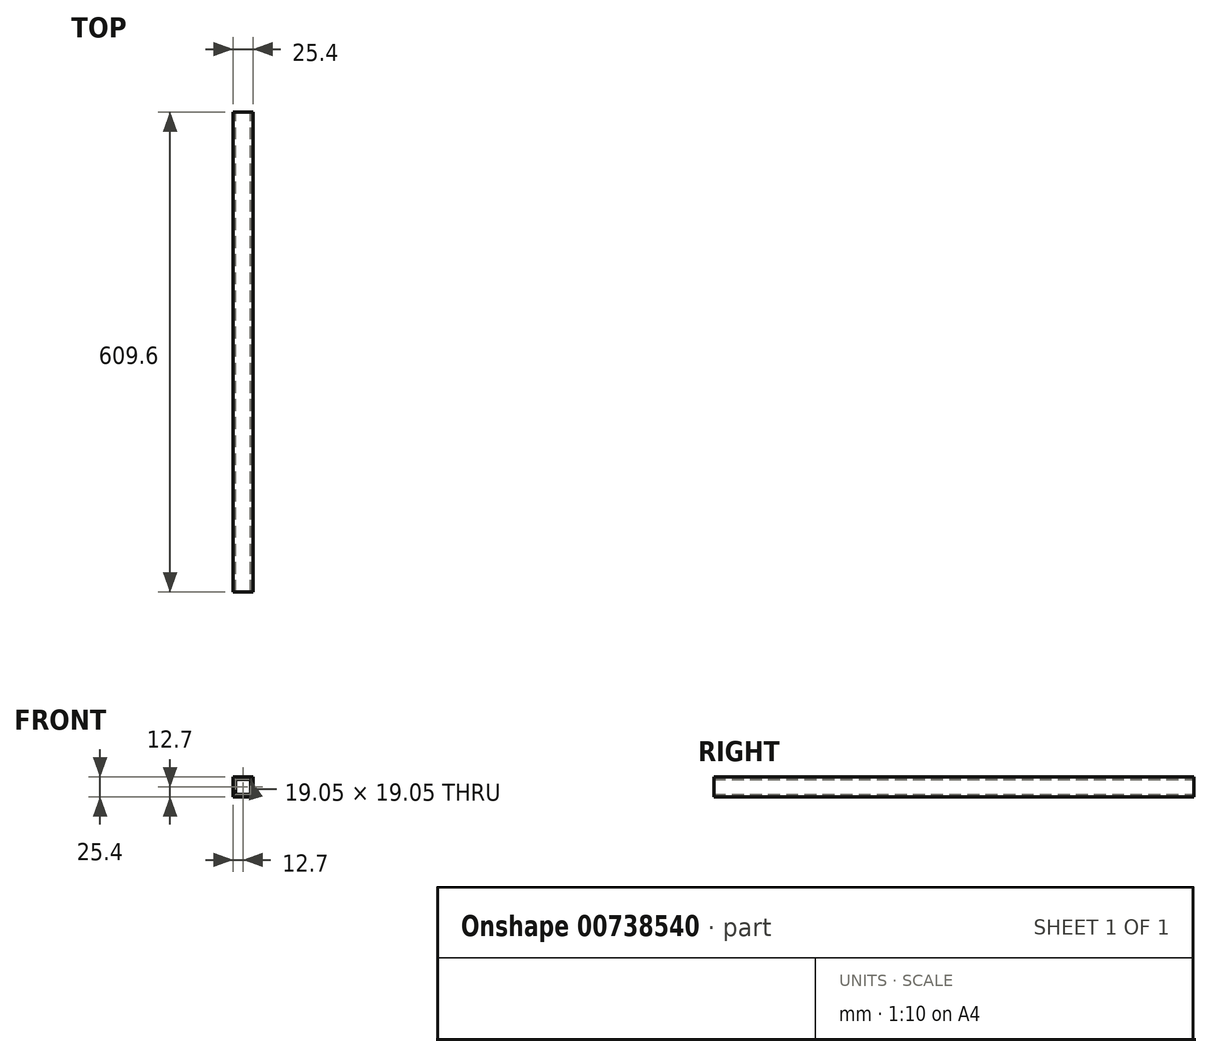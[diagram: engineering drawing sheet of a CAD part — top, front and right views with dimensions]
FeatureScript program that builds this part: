
annotation { "Feature Type Name" : "Feature", "Feature Type Description" : "" }
export const myFeature = defineFeature(function(context is Context, id is Id, definition is map)
    precondition{}
    {
        {
            var Q0;
            Q0=qCreatedBy(makeId("Front.planeOp"),FACE);
            var sketch = newSketch(context, id + "F0", { "sketchPlane" : qUnion([Q0])});
            skLineSegment(sketch, "E0.bottom", {"start": v(12.7, 12.7) * mm, "end": v(-12.7, 12.7) * mm});
            skLineSegment(sketch, "E0.top", {"start": v(12.7, -12.7) * mm, "end": v(-12.7, -12.7) * mm});
            skLineSegment(sketch, "E0.left", {"start": v(12.7, 12.7) * mm, "end": v(12.7, -12.7) * mm});
            skLineSegment(sketch, "E0.right", {"start": v(-12.7, 12.7) * mm, "end": v(-12.7, -12.7) * mm});
            skPoint(sketch, "E0.middle", {"position": v(0, 0) * mm});
            skLineSegment(sketch, "E1.0", {"start": v(-9.53, 9.53) * mm, "end": v(-9.53, -9.52) * mm});
            skLineSegment(sketch, "E1.1", {"start": v(9.52, 9.53) * mm, "end": v(-9.53, 9.53) * mm});
            skLineSegment(sketch, "E1.2", {"start": v(9.53, 9.53) * mm, "end": v(9.53, -9.52) * mm});
            skLineSegment(sketch, "E1.3", {"start": v(9.53, -9.52) * mm, "end": v(-9.53, -9.52) * mm});
            skSolve(sketch);
        }
        {
            var Q0;
            Q0 = qSketchRegion(id + "F0", true);
            extrude(context, id + "F1", {"entities" : qUnion([Q0]), "depth" : 609.6 * mm, "offsetDistance" : 25.4 * mm});
        }
    });
